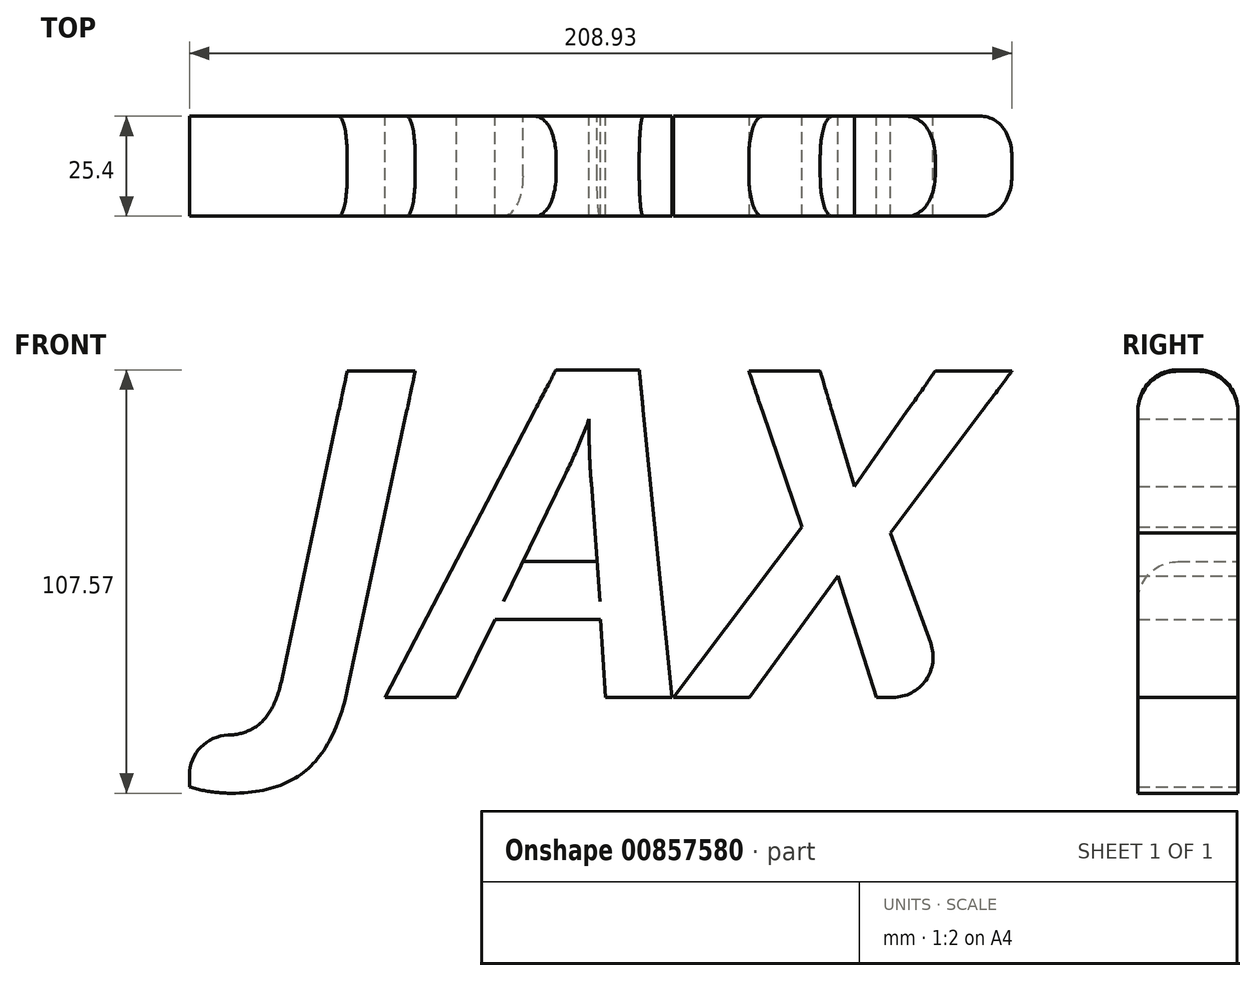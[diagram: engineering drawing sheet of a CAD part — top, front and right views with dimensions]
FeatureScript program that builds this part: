
annotation { "Feature Type Name" : "Feature", "Feature Type Description" : "" }
export const myFeature = defineFeature(function(context is Context, id is Id, definition is map)
    precondition{}
    {
        {
            var Q0;
            Q0=qCreatedBy(makeId("Front.planeOp"),FACE);
            var sketch = newSketch(context, id + "F0", { "sketchPlane" : qUnion([Q0])});
            skText(sketch, "E0", { "text": "JAX\n\n", "fontName": "OpenSans-BoldItalic.ttf"});
            const initialGuessF0  = {"E0": [-0.07068, -0.02178, 1, 0, 0.04178]};
            skSetInitialGuess(sketch, initialGuessF0);
            skSolve(sketch);
        }
        {
            var Q0;
            Q0 = qSketchRegion(id + "F0", true);
            extrude(context, id + "F1", {"entities" : qUnion([Q0]), "depth" : 12.7 * mm, "offsetDistance" : 25.4 * mm});
        }
        {
            var Q0;
            Q0=makeQuery(id+"F1.opExtrude","CAP_EDGE",EDGE,{"disambiguationData":[OSD([sQuery(id+"F0.wireOp",EDGE,"E0.sketch_text.stroke-6")])],"isStart":false});
            var Q1;
            Q1=makeQuery(id+"F1.opExtrude","CAP_EDGE",EDGE,{"disambiguationData":[OSD([sQuery(id+"F0.wireOp",EDGE,"E0.sketch_text.stroke-14")])],"isStart":false});
            var Q2;
            Q2=makeQuery(id+"F1.opExtrude","CAP_EDGE",EDGE,{"disambiguationData":[OSD([sQuery(id+"F0.wireOp",EDGE,"E0.sketch_text.stroke-30")])],"isStart":false});
            var Q3;
            Q3=makeQuery(id+"F1.opExtrude","CAP_EDGE",EDGE,{"disambiguationData":[OSD([sQuery(id+"F0.wireOp",EDGE,"E0.sketch_text.stroke-33")])],"isStart":false});
            var Q4;
            Q4=makeQuery(id+"F1.opExtrude","CAP_EDGE",EDGE,{"disambiguationData":[OSD([sQuery(id+"F0.wireOp",EDGE,"E0.sketch_text.stroke-33")])],"isStart":true});
            var Q5;
            Q5=makeQuery(id+"F1.opExtrude","CAP_EDGE",EDGE,{"disambiguationData":[OSD([sQuery(id+"F0.wireOp",EDGE,"E0.sketch_text.stroke-30")])],"isStart":true});
            var Q6;
            Q6=makeQuery(id+"F1.opExtrude","CAP_EDGE",EDGE,{"disambiguationData":[OSD([sQuery(id+"F0.wireOp",EDGE,"E0.sketch_text.stroke-14")])],"isStart":true});
            var Q7;
            Q7=makeQuery(id+"F1.opExtrude","CAP_EDGE",EDGE,{"disambiguationData":[OSD([sQuery(id+"F0.wireOp",EDGE,"E0.sketch_text.stroke-6")])],"isStart":true});
            var Q8;
            Q8=makeQuery(id+"F1.opExtrude","SWEPT_EDGE",EDGE,{"disambiguationData":[OSD([sQuery(id+"F0.wireOp",EDGE,"E0.sketch_text.stroke-1"),sQuery(id+"F0.wireOp",EDGE,"E0.sketch_text.stroke-2")])]});
            var Q9;
            Q9=makeQuery(id+"F1.opExtrude","CAP_EDGE",EDGE,{"disambiguationData":[OSD([sQuery(id+"F0.wireOp",EDGE,"E0.sketch_text.stroke-23")])],"isStart":false});
            var Q10;
            Q10=makeQuery(id+"F1.opExtrude","SWEPT_EDGE",EDGE,{"disambiguationData":[OSD([sQuery(id+"F0.wireOp",EDGE,"E0.sketch_text.stroke-24"),sQuery(id+"F0.wireOp",EDGE,"E0.sketch_text.stroke-35")])]});
            fillet(context, id + "F2", {"entities" : qUnion([Q0, Q1, Q2, Q3, Q4, Q5, Q6, Q7, Q8, Q9, Q10]), "radius" : 5.08 * mm, "tangentPropagation" : true, "allowEdgeOverflow" : false});
        }
        {
            var Q0;
            Q0=makeQuery(id+"F1.opExtrude","SWEPT_BODY",BODY,{"disambiguationData":[OSD([sQuery(id+"F0.wireOp",EDGE,"E0.sketch_text.stroke-0"),sQuery(id+"F0.wireOp",EDGE,"E0.sketch_text.stroke-1"),sQuery(id+"F0.wireOp",EDGE,"E0.sketch_text.stroke-2"),sQuery(id+"F0.wireOp",EDGE,"E0.sketch_text.stroke-3"),sQuery(id+"F0.wireOp",EDGE,"E0.sketch_text.stroke-4"),sQuery(id+"F0.wireOp",EDGE,"E0.sketch_text.stroke-5"),sQuery(id+"F0.wireOp",EDGE,"E0.sketch_text.stroke-6"),sQuery(id+"F0.wireOp",EDGE,"E0.sketch_text.stroke-7"),sQuery(id+"F0.wireOp",EDGE,"E0.sketch_text.stroke-8"),sQuery(id+"F0.wireOp",EDGE,"E0.sketch_text.stroke-9")])]});
            var Q1;
            Q1=makeQuery(id+"F1.opExtrude","SWEPT_BODY",BODY,{"disambiguationData":[OSD([sQuery(id+"F0.wireOp",EDGE,"E0.sketch_text.stroke-10"),sQuery(id+"F0.wireOp",EDGE,"E0.sketch_text.stroke-11"),sQuery(id+"F0.wireOp",EDGE,"E0.sketch_text.stroke-12"),sQuery(id+"F0.wireOp",EDGE,"E0.sketch_text.stroke-13"),sQuery(id+"F0.wireOp",EDGE,"E0.sketch_text.stroke-14"),sQuery(id+"F0.wireOp",EDGE,"E0.sketch_text.stroke-15"),sQuery(id+"F0.wireOp",EDGE,"E0.sketch_text.stroke-16"),sQuery(id+"F0.wireOp",EDGE,"E0.sketch_text.stroke-17"),sQuery(id+"F0.wireOp",EDGE,"E0.sketch_text.stroke-18"),sQuery(id+"F0.wireOp",EDGE,"E0.sketch_text.stroke-19"),sQuery(id+"F0.wireOp",EDGE,"E0.sketch_text.stroke-20"),sQuery(id+"F0.wireOp",EDGE,"E0.sketch_text.stroke-21"),sQuery(id+"F0.wireOp",EDGE,"E0.sketch_text.stroke-22"),sQuery(id+"F0.wireOp",EDGE,"E0.sketch_text.stroke-23")])]});
            var Q2;
            Q2=makeQuery(id+"F1.opExtrude","SWEPT_BODY",BODY,{"disambiguationData":[OSD([sQuery(id+"F0.wireOp",EDGE,"E0.sketch_text.stroke-24"),sQuery(id+"F0.wireOp",EDGE,"E0.sketch_text.stroke-25"),sQuery(id+"F0.wireOp",EDGE,"E0.sketch_text.stroke-26"),sQuery(id+"F0.wireOp",EDGE,"E0.sketch_text.stroke-27"),sQuery(id+"F0.wireOp",EDGE,"E0.sketch_text.stroke-28"),sQuery(id+"F0.wireOp",EDGE,"E0.sketch_text.stroke-29"),sQuery(id+"F0.wireOp",EDGE,"E0.sketch_text.stroke-30"),sQuery(id+"F0.wireOp",EDGE,"E0.sketch_text.stroke-31"),sQuery(id+"F0.wireOp",EDGE,"E0.sketch_text.stroke-32"),sQuery(id+"F0.wireOp",EDGE,"E0.sketch_text.stroke-33"),sQuery(id+"F0.wireOp",EDGE,"E0.sketch_text.stroke-34"),sQuery(id+"F0.wireOp",EDGE,"E0.sketch_text.stroke-35")])]});
            var Q3;
            Q3=qCreatedBy(makeId("Origin.pointOp"),VERTEX);
            transform(context, id + "F3", {"entities" : qUnion([Q0, Q1, Q2]), "transformType" : TransformType.SCALE_UNIFORMLY, "scale" : 2, "scalePoint" : qUnion([Q3]), "makeCopy" : false});
        }
    });
